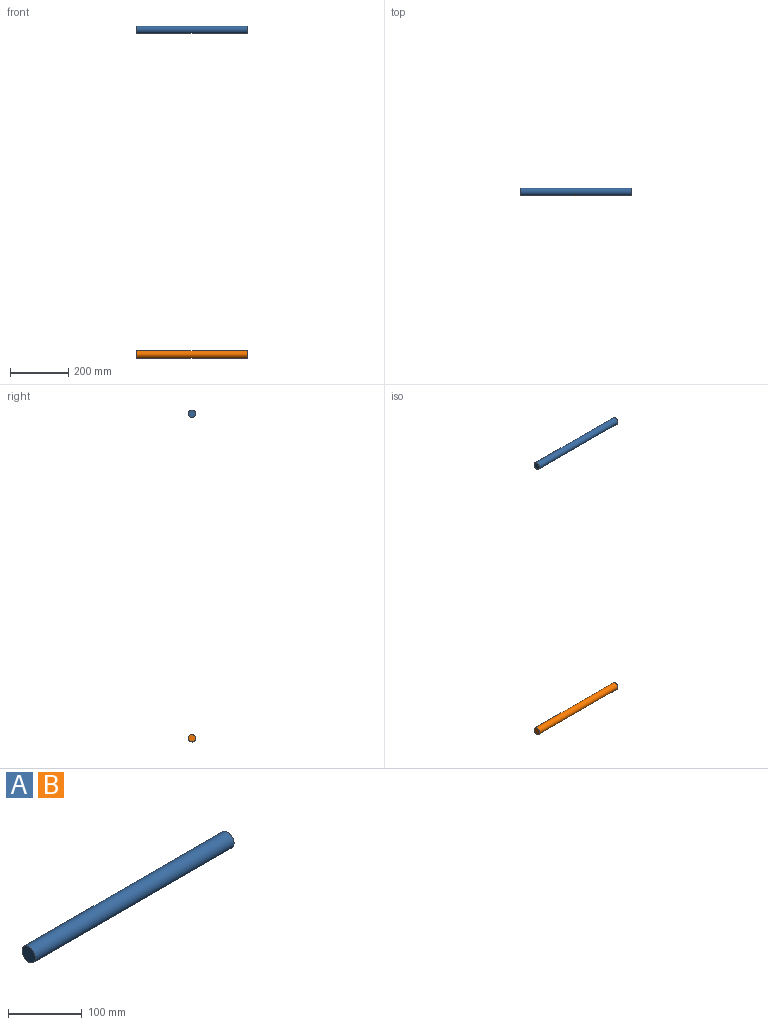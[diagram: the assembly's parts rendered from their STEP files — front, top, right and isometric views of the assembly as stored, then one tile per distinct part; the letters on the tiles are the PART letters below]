
ASSEMBLY  parts=2 mates=1
PART A: 3 faces, bbox 381x25.4x25.4 mm
  f0: cylinder r=12.7mm len=381mm, axis (-1,0,0), area 30402.4mm2, adj f1,f2
  f1: plane 25.4x25.4mm, normal (1,0,0), area 506.7mm2, adj f0
  f2: plane 25.4x25.4mm, normal (-1,0,0), area 506.7mm2, adj f0
PART B: same geometry as A
PLACE A t=(0,0,518.05)mm
PLACE B t=(0,0,-597.07)mm
MATE planar A.f0 <-> B.f0  axis (1,0,0) through (381,0,591)mm
